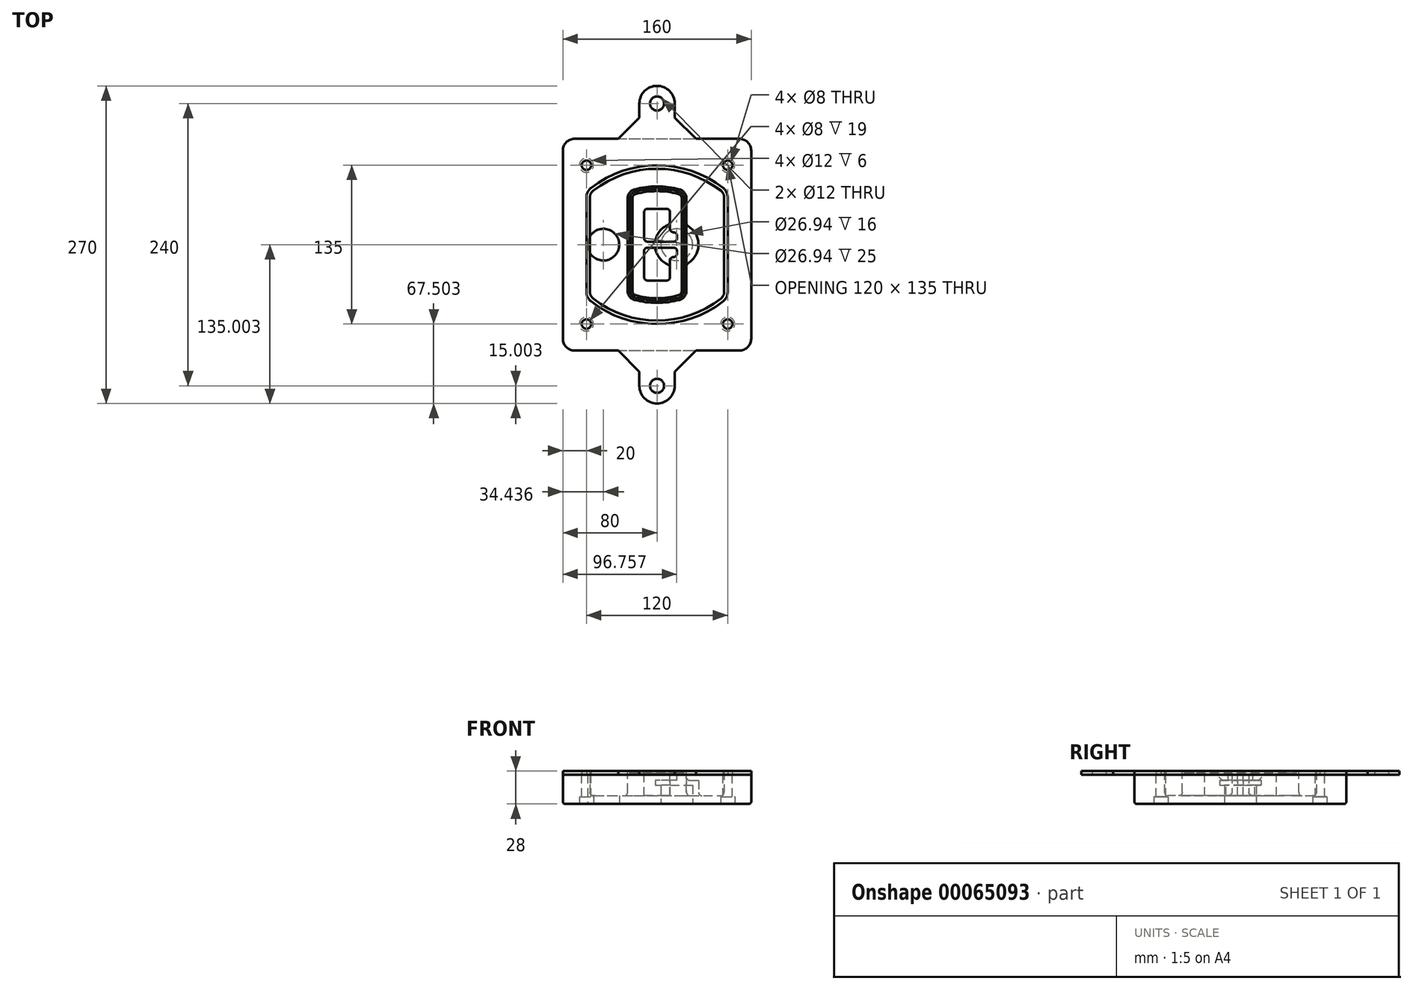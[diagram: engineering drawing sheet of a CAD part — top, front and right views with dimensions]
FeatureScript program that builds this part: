
annotation { "Feature Type Name" : "Feature", "Feature Type Description" : "" }
export const myFeature = defineFeature(function(context is Context, id is Id, definition is map)
    precondition{}
    {
        {
            var Q0;
            Q0=qCreatedBy(makeId("Top.planeOp"),FACE);
            var sketch = newSketch(context, id + "F0", { "sketchPlane" : qUnion([Q0])});
            skPoint(sketch, "E0.rect.middle", {"position": v(0, 0) * mm});
            skLineSegment(sketch, "E1.bottom", {"start": v(24.05, 28.38) * mm, "end": v(164.05, 28.38) * mm});
            skLineSegment(sketch, "E1.top", {"start": v(24.05, 208.38) * mm, "end": v(164.05, 208.38) * mm});
            skLineSegment(sketch, "E1.left", {"start": v(14.05, 38.38) * mm, "end": v(14.05, 198.38) * mm});
            skLineSegment(sketch, "E1.right", {"start": v(174.05, 38.38) * mm, "end": v(174.05, 198.38) * mm});
            skLineSegment(sketch, "E2", {"start": v(14.05, 208.38) * mm, "end": v(174.05, 28.38) * mm, "construction": true});
            skLineSegment(sketch, "E3", {"start": v(174.05, 208.38) * mm, "end": v(14.05, 28.38) * mm, "construction": true});
            skCircle(sketch, "E4", {"center": v(34.05, 185.88) * mm, "radius": 4 * mm});
            skCircle(sketch, "E5", {"center": v(154.05, 185.88) * mm, "radius": 4 * mm});
            skCircle(sketch, "E6", {"center": v(154.05, 50.88) * mm, "radius": 4 * mm});
            skCircle(sketch, "E7", {"center": v(34.05, 50.88) * mm, "radius": 4 * mm});
            skLineSegment(sketch, "E8", {"start": v(34.05, 185.88) * mm, "end": v(154.05, 185.88) * mm, "construction": true});
            skLineSegment(sketch, "E9", {"start": v(154.05, 185.88) * mm, "end": v(154.05, 50.88) * mm, "construction": true});
            skLineSegment(sketch, "E10", {"start": v(154.05, 50.88) * mm, "end": v(34.05, 50.88) * mm, "construction": true});
            skLineSegment(sketch, "E11", {"start": v(34.05, 50.88) * mm, "end": v(34.05, 185.88) * mm, "construction": true});
            skLineSegment(sketch, "E12", {"start": v(34.05, 158.68) * mm, "end": v(34.05, 78.09) * mm});
            skLineSegment(sketch, "E13", {"start": v(154.05, 158.68) * mm, "end": v(154.05, 78.09) * mm});
            skArc(sketch, "E14", {"start": v(150.2, 166.56) * mm, "mid": v(94.05, 185.88) * mm, "end": v(37.9, 166.56) * mm});
            skArc(sketch, "E15", {"start": v(37.9, 70.2) * mm, "mid": v(94.05, 50.88) * mm, "end": v(150.2, 70.2) * mm});
            skLineSegment(sketch, "E16", {"start": v(34.05, 118.38) * mm, "end": v(154.05, 118.38) * mm, "construction": true});
            skPoint(sketch, "E17.visualSharp", {"position": v(34.05, 73.38) * mm});
            skArc(sketch, "E17.filletArc", {"start": v(34.05, 78.09) * mm, "mid": v(35.06, 73.7) * mm, "end": v(37.9, 70.2) * mm});
            skPoint(sketch, "E18.visualSharp", {"position": v(34.05, 163.38) * mm});
            skArc(sketch, "E18.filletArc", {"start": v(37.9, 166.56) * mm, "mid": v(35.06, 163.06) * mm, "end": v(34.05, 158.68) * mm});
            skPoint(sketch, "E19.visualSharp", {"position": v(154.05, 163.38) * mm});
            skArc(sketch, "E19.filletArc", {"start": v(154.05, 158.68) * mm, "mid": v(153.04, 163.06) * mm, "end": v(150.2, 166.56) * mm});
            skPoint(sketch, "E20.visualSharp", {"position": v(154.05, 73.38) * mm});
            skArc(sketch, "E20.filletArc", {"start": v(150.2, 70.2) * mm, "mid": v(153.04, 73.7) * mm, "end": v(154.05, 78.09) * mm});
            skPoint(sketch, "E21.visualSharp", {"position": v(14.05, 208.38) * mm});
            skArc(sketch, "E21.filletArc", {"start": v(24.05, 208.38) * mm, "mid": v(16.98, 205.45) * mm, "end": v(14.05, 198.38) * mm});
            skPoint(sketch, "E22.visualSharp", {"position": v(174.05, 208.38) * mm});
            skArc(sketch, "E22.filletArc", {"start": v(174.05, 198.38) * mm, "mid": v(171.12, 205.45) * mm, "end": v(164.05, 208.38) * mm});
            skPoint(sketch, "E23.visualSharp", {"position": v(174.05, 28.38) * mm});
            skArc(sketch, "E23.filletArc", {"start": v(164.05, 28.38) * mm, "mid": v(171.12, 31.31) * mm, "end": v(174.05, 38.38) * mm});
            skPoint(sketch, "E24.visualSharp", {"position": v(14.05, 28.38) * mm});
            skArc(sketch, "E24.filletArc", {"start": v(14.05, 38.38) * mm, "mid": v(16.98, 31.31) * mm, "end": v(24.05, 28.38) * mm});
            skArc(sketch, "E25.0", {"start": v(151.05, 158.68) * mm, "mid": v(150.34, 161.75) * mm, "end": v(148.36, 164.2) * mm});
            skLineSegment(sketch, "E25.1", {"start": v(151.05, 158.68) * mm, "end": v(151.05, 78.09) * mm});
            skArc(sketch, "E25.2", {"start": v(148.36, 72.57) * mm, "mid": v(150.34, 75.02) * mm, "end": v(151.05, 78.09) * mm});
            skArc(sketch, "E25.3", {"start": v(39.74, 72.57) * mm, "mid": v(94.05, 53.88) * mm, "end": v(148.36, 72.57) * mm});
            skArc(sketch, "E25.4", {"start": v(37.05, 78.09) * mm, "mid": v(37.76, 75.02) * mm, "end": v(39.74, 72.57) * mm});
            skArc(sketch, "E25.5", {"start": v(148.36, 164.2) * mm, "mid": v(94.05, 182.88) * mm, "end": v(39.74, 164.2) * mm});
            skLineSegment(sketch, "E25.6", {"start": v(37.05, 158.68) * mm, "end": v(37.05, 78.09) * mm});
            skArc(sketch, "E25.7", {"start": v(39.74, 164.2) * mm, "mid": v(37.76, 161.75) * mm, "end": v(37.05, 158.68) * mm});
            skArc(sketch, "E26.0", {"start": v(35.43, 169.71) * mm, "mid": v(31.47, 164.82) * mm, "end": v(30.05, 158.68) * mm});
            skArc(sketch, "E26.1", {"start": v(152.67, 169.71) * mm, "mid": v(94.05, 189.88) * mm, "end": v(35.43, 169.71) * mm});
            skArc(sketch, "E26.2", {"start": v(158.05, 158.68) * mm, "mid": v(156.63, 164.82) * mm, "end": v(152.67, 169.71) * mm});
            skLineSegment(sketch, "E26.3", {"start": v(158.05, 158.68) * mm, "end": v(158.05, 78.09) * mm});
            skArc(sketch, "E26.4", {"start": v(152.67, 67.05) * mm, "mid": v(156.63, 71.95) * mm, "end": v(158.05, 78.09) * mm});
            skLineSegment(sketch, "E26.5", {"start": v(30.05, 158.68) * mm, "end": v(30.05, 78.09) * mm});
            skArc(sketch, "E26.6", {"start": v(35.43, 67.05) * mm, "mid": v(94.05, 46.88) * mm, "end": v(152.67, 67.05) * mm});
            skArc(sketch, "E26.7", {"start": v(30.05, 78.09) * mm, "mid": v(31.47, 71.95) * mm, "end": v(35.43, 67.05) * mm});
            skSolve(sketch);
        }
        {
            var Q0;
            Q0=makeQuery(id+"F0.imprint","IMPRINT",FACE,{"disambiguationData":[TD([[makeQuery(id+"F0.imprint","IMPRINT",EDGE,{"derivedFrom":sQuery(id+"F0.wireOp",EDGE,"E1.bottom")}),1.0]])]});
            var Q1;
            Q1=makeQuery(id+"F0.imprint","IMPRINT",FACE,{"disambiguationData":[TD([[makeQuery(id+"F0.imprint","IMPRINT",EDGE,{"derivedFrom":sQuery(id+"F0.wireOp",EDGE,"E12")}),1.0]])]});
            var Q2;
            Q2=makeQuery(id+"F0.imprint","IMPRINT",FACE,{"disambiguationData":[TD([[makeQuery(id+"F0.imprint","IMPRINT",EDGE,{"derivedFrom":sQuery(id+"F0.wireOp",EDGE,"E25.0")}),1.0]])]});
            var Q3;
            Q3=makeQuery(id+"F0.imprint","IMPRINT",FACE,{"disambiguationData":[TD([[makeQuery(id+"F0.imprint","IMPRINT",EDGE,{"derivedFrom":sQuery(id+"F0.wireOp",EDGE,"E12")}),-1.0]])]});
            extrude(context, id + "F1", {"entities" : qUnion([Q0, Q1, Q2, Q3]), "oppositeDirection" : true, "depth" : 25 * mm});
        }
        {
            var Q0;
            Q0=makeQuery(id+"F0.imprint","IMPRINT",FACE,{"disambiguationData":[TD([[makeQuery(id+"F0.imprint","IMPRINT",EDGE,{"derivedFrom":sQuery(id+"F0.wireOp",EDGE,"E12")}),1.0]])]});
            extrude(context, id + "F2", {"entities" : qUnion([Q0]), "operationType" : NewBodyOperationType.ADD, "depth" : 3 * mm});
        }
        {
            var Q0;
            Q0=makeQuery(id+"F0.imprint","IMPRINT",FACE,{"disambiguationData":[TD([[makeQuery(id+"F0.imprint","IMPRINT",EDGE,{"derivedFrom":sQuery(id+"F0.wireOp",EDGE,"E25.0")}),1.0]])]});
            extrude(context, id + "F3", {"entities" : qUnion([Q0]), "operationType" : NewBodyOperationType.REMOVE, "oppositeDirection" : true, "depth" : 18 * mm});
        }
        {
            var Q0;
            Q0=makeQuery(id+"F2.opExtrude","CAP_FACE",FACE,{"disambiguationData":[OSD([sQuery(id+"F0.wireOp",EDGE,"E12"),sQuery(id+"F0.wireOp",EDGE,"E13"),sQuery(id+"F0.wireOp",EDGE,"E14"),sQuery(id+"F0.wireOp",EDGE,"E15"),sQuery(id+"F0.wireOp",EDGE,"E17.filletArc"),sQuery(id+"F0.wireOp",EDGE,"E18.filletArc"),sQuery(id+"F0.wireOp",EDGE,"E19.filletArc"),sQuery(id+"F0.wireOp",EDGE,"E20.filletArc"),sQuery(id+"F0.wireOp",EDGE,"E25.0"),sQuery(id+"F0.wireOp",EDGE,"E25.1"),sQuery(id+"F0.wireOp",EDGE,"E25.2"),sQuery(id+"F0.wireOp",EDGE,"E25.3"),sQuery(id+"F0.wireOp",EDGE,"E25.4"),sQuery(id+"F0.wireOp",EDGE,"E25.5"),sQuery(id+"F0.wireOp",EDGE,"E25.6"),sQuery(id+"F0.wireOp",EDGE,"E25.7")])],"isStart":false});
            var sketch = newSketch(context, id + "F4", { "sketchPlane" : qUnion([Q0])});
            skArc(sketch, "E27.0", {"start": v(74.97, 71.41) * mm, "mid": v(94.05, 68.88) * mm, "end": v(113.13, 71.41) * mm});
            skArc(sketch, "E28.0", {"start": v(113.13, 165.35) * mm, "mid": v(94.05, 167.88) * mm, "end": v(74.97, 165.35) * mm});
            skLineSegment(sketch, "E29", {"start": v(69.05, 157.63) * mm, "end": v(69.05, 79.14) * mm});
            skLineSegment(sketch, "E30", {"start": v(119.05, 157.63) * mm, "end": v(119.05, 79.14) * mm});
            skLineSegment(sketch, "E31", {"start": v(69.05, 163.48) * mm, "end": v(119.05, 163.48) * mm, "construction": true});
            skLineSegment(sketch, "E32", {"start": v(69.05, 73.28) * mm, "end": v(119.05, 73.28) * mm, "construction": true});
            skPoint(sketch, "E33.visualSharp", {"position": v(69.05, 163.48) * mm});
            skArc(sketch, "E33.filletArc", {"start": v(74.97, 165.35) * mm, "mid": v(70.7, 162.5) * mm, "end": v(69.05, 157.63) * mm});
            skPoint(sketch, "E34.visualSharp", {"position": v(119.05, 163.48) * mm});
            skArc(sketch, "E34.filletArc", {"start": v(119.05, 157.63) * mm, "mid": v(117.4, 162.5) * mm, "end": v(113.13, 165.35) * mm});
            skPoint(sketch, "E35.visualSharp", {"position": v(119.05, 73.28) * mm});
            skArc(sketch, "E35.filletArc", {"start": v(113.13, 71.41) * mm, "mid": v(117.4, 74.27) * mm, "end": v(119.05, 79.14) * mm});
            skPoint(sketch, "E36.visualSharp", {"position": v(69.05, 73.28) * mm});
            skArc(sketch, "E36.filletArc", {"start": v(69.05, 79.14) * mm, "mid": v(70.7, 74.27) * mm, "end": v(74.97, 71.41) * mm});
            skArc(sketch, "E37.0", {"start": v(148.36, 164.2) * mm, "mid": v(94.05, 182.88) * mm, "end": v(39.74, 164.2) * mm});
            skArc(sketch, "E37.1", {"start": v(39.74, 164.2) * mm, "mid": v(37.76, 161.75) * mm, "end": v(37.05, 158.68) * mm});
            skLineSegment(sketch, "E37.2", {"start": v(37.05, 158.68) * mm, "end": v(37.05, 78.09) * mm});
            skArc(sketch, "E37.3", {"start": v(37.05, 78.09) * mm, "mid": v(37.76, 75.02) * mm, "end": v(39.74, 72.57) * mm});
            skArc(sketch, "E37.4", {"start": v(39.74, 72.57) * mm, "mid": v(94.05, 53.88) * mm, "end": v(148.36, 72.57) * mm});
            skArc(sketch, "E37.5", {"start": v(148.36, 72.57) * mm, "mid": v(150.34, 75.02) * mm, "end": v(151.05, 78.09) * mm});
            skLineSegment(sketch, "E37.6", {"start": v(151.05, 158.68) * mm, "end": v(151.05, 78.09) * mm});
            skArc(sketch, "E37.7", {"start": v(151.05, 158.68) * mm, "mid": v(150.34, 161.75) * mm, "end": v(148.36, 164.2) * mm});
            skLineSegment(sketch, "E38.0", {"start": v(117.05, 157.63) * mm, "end": v(117.05, 79.14) * mm});
            skArc(sketch, "E38.1", {"start": v(112.61, 73.34) * mm, "mid": v(115.81, 75.49) * mm, "end": v(117.05, 79.14) * mm});
            skArc(sketch, "E38.2", {"start": v(75.49, 73.34) * mm, "mid": v(94.05, 70.88) * mm, "end": v(112.61, 73.34) * mm});
            skArc(sketch, "E38.3", {"start": v(71.05, 79.14) * mm, "mid": v(72.29, 75.49) * mm, "end": v(75.49, 73.34) * mm});
            skLineSegment(sketch, "E38.4", {"start": v(71.05, 157.63) * mm, "end": v(71.05, 79.14) * mm});
            skArc(sketch, "E38.5", {"start": v(117.05, 157.63) * mm, "mid": v(115.81, 161.28) * mm, "end": v(112.61, 163.42) * mm});
            skArc(sketch, "E38.6", {"start": v(75.49, 163.42) * mm, "mid": v(72.29, 161.28) * mm, "end": v(71.05, 157.63) * mm});
            skArc(sketch, "E38.7", {"start": v(112.61, 163.42) * mm, "mid": v(94.05, 165.88) * mm, "end": v(75.49, 163.42) * mm});
            skArc(sketch, "E39.0", {"start": v(115.05, 157.63) * mm, "mid": v(114.23, 160.06) * mm, "end": v(112.1, 161.5) * mm});
            skLineSegment(sketch, "E39.1", {"start": v(115.05, 157.63) * mm, "end": v(115.05, 79.14) * mm});
            skArc(sketch, "E39.2", {"start": v(112.1, 75.27) * mm, "mid": v(114.23, 76.7) * mm, "end": v(115.05, 79.14) * mm});
            skArc(sketch, "E39.3", {"start": v(76, 75.27) * mm, "mid": v(94.05, 72.88) * mm, "end": v(112.1, 75.27) * mm});
            skArc(sketch, "E39.4", {"start": v(73.05, 79.14) * mm, "mid": v(73.87, 76.7) * mm, "end": v(76, 75.27) * mm});
            skArc(sketch, "E39.5", {"start": v(112.1, 161.5) * mm, "mid": v(94.05, 163.88) * mm, "end": v(76, 161.5) * mm});
            skLineSegment(sketch, "E39.6", {"start": v(73.05, 157.63) * mm, "end": v(73.05, 79.14) * mm});
            skArc(sketch, "E39.7", {"start": v(76, 161.5) * mm, "mid": v(73.87, 160.06) * mm, "end": v(73.05, 157.63) * mm});
            skLineSegment(sketch, "E40", {"start": v(69.05, 118.38) * mm, "end": v(119.05, 118.38) * mm, "construction": true});
            skLineSegment(sketch, "E41", {"start": v(83.05, 123.88) * mm, "end": v(83.05, 145.88) * mm});
            skLineSegment(sketch, "E42", {"start": v(86.05, 148.88) * mm, "end": v(102.05, 148.88) * mm});
            skLineSegment(sketch, "E43", {"start": v(105.05, 145.88) * mm, "end": v(105.05, 131.88) * mm});
            skLineSegment(sketch, "E44", {"start": v(108.05, 128.88) * mm, "end": v(108.05, 128.88) * mm});
            skLineSegment(sketch, "E45", {"start": v(111.05, 125.88) * mm, "end": v(111.05, 123.88) * mm});
            skLineSegment(sketch, "E46", {"start": v(108.05, 120.88) * mm, "end": v(86.05, 120.88) * mm});
            skPoint(sketch, "E47.visualSharp", {"position": v(83.05, 148.88) * mm});
            skArc(sketch, "E47.filletArc", {"start": v(86.05, 148.88) * mm, "mid": v(83.93, 148) * mm, "end": v(83.05, 145.88) * mm});
            skPoint(sketch, "E48.visualSharp", {"position": v(105.05, 148.88) * mm});
            skArc(sketch, "E48.filletArc", {"start": v(105.05, 145.88) * mm, "mid": v(104.17, 148) * mm, "end": v(102.05, 148.88) * mm});
            skPoint(sketch, "E49.visualSharp", {"position": v(105.05, 128.88) * mm});
            skArc(sketch, "E49.filletArc", {"start": v(105.05, 131.88) * mm, "mid": v(105.93, 129.76) * mm, "end": v(108.05, 128.88) * mm});
            skPoint(sketch, "E50.visualSharp", {"position": v(111.05, 128.88) * mm});
            skArc(sketch, "E50.filletArc", {"start": v(111.05, 125.88) * mm, "mid": v(110.17, 128) * mm, "end": v(108.05, 128.88) * mm});
            skPoint(sketch, "E51.visualSharp", {"position": v(111.05, 120.88) * mm});
            skArc(sketch, "E51.filletArc", {"start": v(108.05, 120.88) * mm, "mid": v(110.17, 121.76) * mm, "end": v(111.05, 123.88) * mm});
            skPoint(sketch, "E52.visualSharp", {"position": v(83.05, 120.88) * mm});
            skArc(sketch, "E52.filletArc", {"start": v(83.05, 123.88) * mm, "mid": v(83.93, 121.76) * mm, "end": v(86.05, 120.88) * mm});
            skLineSegment(sketch, "E53.0.MirrorCS", {"start": v(108.05, 115.88) * mm, "end": v(86.05, 115.88) * mm});
            skArc(sketch, "E54.0.MirrorCS", {"start": v(83.05, 112.88) * mm, "mid": v(83.93, 115) * mm, "end": v(86.05, 115.88) * mm});
            skLineSegment(sketch, "E55.0.MirrorCS", {"start": v(83.05, 112.88) * mm, "end": v(83.05, 90.88) * mm});
            skArc(sketch, "E56.0.MirrorCS", {"start": v(86.05, 87.88) * mm, "mid": v(83.93, 88.76) * mm, "end": v(83.05, 90.88) * mm});
            skLineSegment(sketch, "E57.0.MirrorCS", {"start": v(86.05, 87.88) * mm, "end": v(102.05, 87.88) * mm});
            skArc(sketch, "E58.0.MirrorCS", {"start": v(105.05, 90.88) * mm, "mid": v(104.17, 88.76) * mm, "end": v(102.05, 87.88) * mm});
            skLineSegment(sketch, "E59.0.MirrorCS", {"start": v(105.05, 90.88) * mm, "end": v(105.05, 104.88) * mm});
            skArc(sketch, "E60.0.MirrorCS", {"start": v(105.05, 104.88) * mm, "mid": v(105.93, 107) * mm, "end": v(108.05, 107.88) * mm});
            skArc(sketch, "E61.0.MirrorCS", {"start": v(111.05, 110.88) * mm, "mid": v(110.17, 108.76) * mm, "end": v(108.05, 107.88) * mm});
            skLineSegment(sketch, "E62.0.MirrorCS", {"start": v(111.05, 110.88) * mm, "end": v(111.05, 112.88) * mm});
            skArc(sketch, "E63.0.MirrorCS", {"start": v(108.05, 115.88) * mm, "mid": v(110.17, 115) * mm, "end": v(111.05, 112.88) * mm});
            skSolve(sketch);
        }
        {
            var Q0;
            Q0=makeQuery(id+"F4.imprint","IMPRINT",FACE,{"disambiguationData":[TD([[makeQuery(id+"F4.imprint","IMPRINT",EDGE,{"derivedFrom":sQuery(id+"F4.wireOp",EDGE,"E27.0")}),1.0]])]});
            var Q1;
            Q1=makeQuery(id+"F4.imprint","IMPRINT",FACE,{"disambiguationData":[TD([[makeQuery(id+"F4.imprint","IMPRINT",EDGE,{"derivedFrom":sQuery(id+"F4.wireOp",EDGE,"E38.0")}),-1.0]])]});
            var Q2;
            Q2=makeQuery(id+"F4.imprint","IMPRINT",FACE,{"disambiguationData":[TD([[makeQuery(id+"F4.imprint","IMPRINT",EDGE,{"derivedFrom":sQuery(id+"F4.wireOp",EDGE,"E39.0")}),1.0]])]});
            extrude(context, id + "F5", {"entities" : qUnion([Q0, Q1, Q2]), "operationType" : NewBodyOperationType.ADD, "endBound" : BoundingType.UP_TO_NEXT, "oppositeDirection" : true, "depth" : 25 * mm});
        }
        {
            var Q0;
            Q0=makeQuery(id+"F4.imprint","IMPRINT",FACE,{"disambiguationData":[TD([[makeQuery(id+"F4.imprint","IMPRINT",EDGE,{"derivedFrom":sQuery(id+"F4.wireOp",EDGE,"E38.0")}),-1.0]])]});
            extrude(context, id + "F6", {"entities" : qUnion([Q0]), "operationType" : NewBodyOperationType.REMOVE, "oppositeDirection" : true, "depth" : 2 * mm});
        }
        {
            var Q0;
            Q0=makeQuery(id+"F1.opExtrude","CAP_FACE",FACE,{"disambiguationData":[OSD([sQuery(id+"F0.wireOp",EDGE,"E1.bottom"),sQuery(id+"F0.wireOp",EDGE,"E1.top"),sQuery(id+"F0.wireOp",EDGE,"E1.left"),sQuery(id+"F0.wireOp",EDGE,"E1.right"),sQuery(id+"F0.wireOp",EDGE,"E4"),sQuery(id+"F0.wireOp",EDGE,"E5"),sQuery(id+"F0.wireOp",EDGE,"E6"),sQuery(id+"F0.wireOp",EDGE,"E7"),sQuery(id+"F0.wireOp",EDGE,"E21.filletArc"),sQuery(id+"F0.wireOp",EDGE,"E22.filletArc"),sQuery(id+"F0.wireOp",EDGE,"E23.filletArc"),sQuery(id+"F0.wireOp",EDGE,"E24.filletArc")])],"isStart":false});
            var sketch = newSketch(context, id + "F7", { "sketchPlane" : qUnion([Q0])});
            skCircle(sketch, "E64", {"center": v(110.8, -118.38) * mm, "radius": 13.47 * mm});
            skCircle(sketch, "E65", {"center": v(48.49, -118.38) * mm, "radius": 13.47 * mm});
            skLineSegment(sketch, "E66", {"start": v(174.05, -118.38) * mm, "end": v(14.05, -118.38) * mm});
            skCircle(sketch, "E67", {"center": v(110.8, -118.38) * mm, "radius": 18.47 * mm});
            skCircle(sketch, "E68", {"center": v(154.05, -185.88) * mm, "radius": 6 * mm});
            skCircle(sketch, "E69", {"center": v(34.05, -185.88) * mm, "radius": 6 * mm});
            skCircle(sketch, "E70", {"center": v(34.05, -50.88) * mm, "radius": 6 * mm});
            skCircle(sketch, "E71", {"center": v(154.05, -50.88) * mm, "radius": 6 * mm});
            skSolve(sketch);
        }
        {
            var Q0;
            {var subQ1=sQuery(id+"F7.wireOp",EDGE,"E66");var subQ4=sQuery(id+"F7.wireOp",EDGE,"E64");var subQ6=makeQuery(id+"F7.imprint","INTERSECT",VERTEX,{"disambiguationData":[OD(0.0)],"derivedFrom":[subQ4,subQ1]});Q0=makeQuery(id+"F7.imprint","IMPRINT",FACE,{"disambiguationData":[TD([[makeQuery(id+"F7.imprint","IMPRINT",EDGE,{"disambiguationData":[TD([[subQ6,-1.0]])],"derivedFrom":subQ4}),-1.0]])]});}
            var Q1;
            {var subQ0=sQuery(id+"F7.wireOp",EDGE,"E66");var subQ1=sQuery(id+"F7.wireOp",EDGE,"E64");var subQ3=makeQuery(id+"F7.imprint","INTERSECT",VERTEX,{"disambiguationData":[OD(0.0)],"derivedFrom":[subQ1,subQ0]});Q1=makeQuery(id+"F7.imprint","IMPRINT",FACE,{"disambiguationData":[TD([[makeQuery(id+"F7.imprint","IMPRINT",EDGE,{"disambiguationData":[TD([[subQ3,-1.0]])],"derivedFrom":subQ1}),1.0]])]});}
            var Q2;
            {var subQ0=sQuery(id+"F7.wireOp",EDGE,"E66");var subQ1=sQuery(id+"F7.wireOp",EDGE,"E64");var subQ3=makeQuery(id+"F7.imprint","INTERSECT",VERTEX,{"disambiguationData":[OD(0.0)],"derivedFrom":[subQ1,subQ0]});Q2=makeQuery(id+"F7.imprint","IMPRINT",FACE,{"disambiguationData":[TD([[makeQuery(id+"F7.imprint","IMPRINT",EDGE,{"disambiguationData":[TD([[subQ3,1.0]])],"derivedFrom":subQ1}),1.0]])]});}
            var Q3;
            {var subQ1=sQuery(id+"F7.wireOp",EDGE,"E66");var subQ4=sQuery(id+"F7.wireOp",EDGE,"E64");var subQ6=makeQuery(id+"F7.imprint","INTERSECT",VERTEX,{"disambiguationData":[OD(0.0)],"derivedFrom":[subQ4,subQ1]});Q3=makeQuery(id+"F7.imprint","IMPRINT",FACE,{"disambiguationData":[TD([[makeQuery(id+"F7.imprint","IMPRINT",EDGE,{"disambiguationData":[TD([[subQ6,1.0]])],"derivedFrom":subQ4}),-1.0]])]});}
            extrude(context, id + "F8", {"entities" : qUnion([Q0, Q1, Q2, Q3]), "operationType" : NewBodyOperationType.ADD, "oppositeDirection" : true, "depth" : 20 * mm});
        }
        {
            var Q0;
            {var subQ0=sQuery(id+"F7.wireOp",EDGE,"E66");var subQ1=sQuery(id+"F7.wireOp",EDGE,"E64");var subQ3=makeQuery(id+"F7.imprint","INTERSECT",VERTEX,{"disambiguationData":[OD(0.0)],"derivedFrom":[subQ1,subQ0]});Q0=makeQuery(id+"F7.imprint","IMPRINT",FACE,{"disambiguationData":[TD([[makeQuery(id+"F7.imprint","IMPRINT",EDGE,{"disambiguationData":[TD([[subQ3,-1.0]])],"derivedFrom":subQ1}),1.0]])]});}
            var Q1;
            {var subQ0=sQuery(id+"F7.wireOp",EDGE,"E66");var subQ1=sQuery(id+"F7.wireOp",EDGE,"E64");var subQ3=makeQuery(id+"F7.imprint","INTERSECT",VERTEX,{"disambiguationData":[OD(0.0)],"derivedFrom":[subQ1,subQ0]});Q1=makeQuery(id+"F7.imprint","IMPRINT",FACE,{"disambiguationData":[TD([[makeQuery(id+"F7.imprint","IMPRINT",EDGE,{"disambiguationData":[TD([[subQ3,1.0]])],"derivedFrom":subQ1}),1.0]])]});}
            extrude(context, id + "F9", {"entities" : qUnion([Q0, Q1]), "operationType" : NewBodyOperationType.REMOVE, "oppositeDirection" : true, "depth" : 16 * mm});
        }
        {
            var Q0;
            {var subQ0=sQuery(id+"F7.wireOp",EDGE,"E66");var subQ1=sQuery(id+"F7.wireOp",EDGE,"E65");var subQ3=makeQuery(id+"F7.imprint","INTERSECT",VERTEX,{"disambiguationData":[OD(0.0)],"derivedFrom":[subQ1,subQ0]});Q0=makeQuery(id+"F7.imprint","IMPRINT",FACE,{"disambiguationData":[TD([[makeQuery(id+"F7.imprint","IMPRINT",EDGE,{"disambiguationData":[TD([[subQ3,-1.0]])],"derivedFrom":subQ1}),1.0]])]});}
            var Q1;
            {var subQ0=sQuery(id+"F7.wireOp",EDGE,"E66");var subQ1=sQuery(id+"F7.wireOp",EDGE,"E65");var subQ3=makeQuery(id+"F7.imprint","INTERSECT",VERTEX,{"disambiguationData":[OD(0.0)],"derivedFrom":[subQ1,subQ0]});Q1=makeQuery(id+"F7.imprint","IMPRINT",FACE,{"disambiguationData":[TD([[makeQuery(id+"F7.imprint","IMPRINT",EDGE,{"disambiguationData":[TD([[subQ3,1.0]])],"derivedFrom":subQ1}),1.0]])]});}
            extrude(context, id + "F10", {"entities" : qUnion([Q0, Q1]), "operationType" : NewBodyOperationType.REMOVE, "oppositeDirection" : true, "depth" : 25 * mm});
        }
        {
            var Q0;
            Q0=makeQuery(id+"F7.imprint","IMPRINT",FACE,{"disambiguationData":[TD([[makeQuery(id+"F7.imprint","IMPRINT",EDGE,{"derivedFrom":sQuery(id+"F7.wireOp",EDGE,"E68")}),1.0]])]});
            var Q1;
            Q1=makeQuery(id+"F7.imprint","IMPRINT",FACE,{"disambiguationData":[TD([[makeQuery(id+"F7.imprint","IMPRINT",EDGE,{"derivedFrom":makeQuery(id+"F1.opExtrude","CAP_EDGE",EDGE,{"disambiguationData":[OSD([sQuery(id+"F0.wireOp",EDGE,"E5")])],"isStart":false})}),-1.0]])]});
            var Q2;
            Q2=makeQuery(id+"F7.imprint","IMPRINT",FACE,{"disambiguationData":[TD([[makeQuery(id+"F7.imprint","IMPRINT",EDGE,{"derivedFrom":sQuery(id+"F7.wireOp",EDGE,"E69")}),1.0]])]});
            var Q3;
            Q3=makeQuery(id+"F7.imprint","IMPRINT",FACE,{"disambiguationData":[TD([[makeQuery(id+"F7.imprint","IMPRINT",EDGE,{"derivedFrom":makeQuery(id+"F1.opExtrude","CAP_EDGE",EDGE,{"disambiguationData":[OSD([sQuery(id+"F0.wireOp",EDGE,"E4")])],"isStart":false})}),-1.0]])]});
            var Q4;
            Q4=makeQuery(id+"F7.imprint","IMPRINT",FACE,{"disambiguationData":[TD([[makeQuery(id+"F7.imprint","IMPRINT",EDGE,{"derivedFrom":sQuery(id+"F7.wireOp",EDGE,"E70")}),1.0]])]});
            var Q5;
            Q5=makeQuery(id+"F7.imprint","IMPRINT",FACE,{"disambiguationData":[TD([[makeQuery(id+"F7.imprint","IMPRINT",EDGE,{"derivedFrom":makeQuery(id+"F1.opExtrude","CAP_EDGE",EDGE,{"disambiguationData":[OSD([sQuery(id+"F0.wireOp",EDGE,"E7")])],"isStart":false})}),-1.0]])]});
            var Q6;
            Q6=makeQuery(id+"F7.imprint","IMPRINT",FACE,{"disambiguationData":[TD([[makeQuery(id+"F7.imprint","IMPRINT",EDGE,{"derivedFrom":sQuery(id+"F7.wireOp",EDGE,"E71")}),1.0]])]});
            var Q7;
            Q7=makeQuery(id+"F7.imprint","IMPRINT",FACE,{"disambiguationData":[TD([[makeQuery(id+"F7.imprint","IMPRINT",EDGE,{"derivedFrom":makeQuery(id+"F1.opExtrude","CAP_EDGE",EDGE,{"disambiguationData":[OSD([sQuery(id+"F0.wireOp",EDGE,"E6")])],"isStart":false})}),-1.0]])]});
            extrude(context, id + "F11", {"entities" : qUnion([Q0, Q1, Q2, Q3, Q4, Q5, Q6, Q7]), "operationType" : NewBodyOperationType.REMOVE, "oppositeDirection" : true, "depth" : 6 * mm});
        }
        {
            var Q0;
            Q0=makeQuery(id+"F9.boolean.opBoolean","COPY",FACE,{"derivedFrom":makeQuery(id+"F9.opExtrude","CAP_FACE",FACE,{"disambiguationData":[OSD([sQuery(id+"F7.wireOp",EDGE,"E64")])],"isStart":false})});
            var sketch = newSketch(context, id + "F12", { "sketchPlane" : qUnion([Q0])});
            skArc(sketch, "E72.0", {"start": v(105.05, -100.83) * mm, "mid": v(96.62, -106.56) * mm, "end": v(92.5, -115.88) * mm});
            skArc(sketch, "E72.1", {"start": v(92.5, -120.88) * mm, "mid": v(96.62, -130.2) * mm, "end": v(105.05, -135.93) * mm});
            skLineSegment(sketch, "E73", {"start": v(92.5, -120.88) * mm, "end": v(108.05, -120.88) * mm});
            skLineSegment(sketch, "E74.0", {"start": v(108.05, -115.88) * mm, "end": v(92.5, -115.88) * mm});
            skArc(sketch, "E74.1", {"start": v(108.05, -115.88) * mm, "mid": v(110.17, -115) * mm, "end": v(111.05, -112.88) * mm});
            skLineSegment(sketch, "E74.2", {"start": v(111.05, -110.88) * mm, "end": v(111.05, -112.88) * mm});
            skArc(sketch, "E74.3", {"start": v(111.05, -110.88) * mm, "mid": v(110.17, -108.76) * mm, "end": v(108.05, -107.88) * mm});
            skArc(sketch, "E74.4", {"start": v(105.05, -104.88) * mm, "mid": v(105.93, -107) * mm, "end": v(108.05, -107.88) * mm});
            skLineSegment(sketch, "E74.5", {"start": v(105.05, -100.83) * mm, "end": v(105.05, -104.88) * mm});
            skLineSegment(sketch, "E74.7", {"start": v(108.05, -120.88) * mm, "end": v(92.5, -120.88) * mm});
            skArc(sketch, "E74.8", {"start": v(108.05, -120.88) * mm, "mid": v(110.17, -121.76) * mm, "end": v(111.05, -123.88) * mm});
            skLineSegment(sketch, "E74.9", {"start": v(111.05, -125.88) * mm, "end": v(111.05, -123.88) * mm});
            skArc(sketch, "E74.10", {"start": v(111.05, -125.88) * mm, "mid": v(110.17, -128) * mm, "end": v(108.05, -128.88) * mm});
            skArc(sketch, "E74.11", {"start": v(105.05, -131.88) * mm, "mid": v(105.93, -129.76) * mm, "end": v(108.05, -128.88) * mm});
            skLineSegment(sketch, "E74.12", {"start": v(105.05, -135.93) * mm, "end": v(105.05, -131.88) * mm});
            skPoint(sketch, "E75.orphan", {"position": v(105.05, -145.88) * mm});
            skPoint(sketch, "E76.orphan", {"position": v(86.05, -120.88) * mm});
            skPoint(sketch, "E77.orphan", {"position": v(86.05, -115.88) * mm});
            skPoint(sketch, "E78.orphan", {"position": v(105.05, -90.88) * mm});
            skSolve(sketch);
        }
        {
            var Q0;
            {var subQ7=sQuery(id+"F12.wireOp",EDGE,"E72.0");var subQ14=sQuery(id+"F12.wireOp",EDGE,"E72.1");var subQ16=sQuery(id+"F12.wireOp",EDGE,"E74.1");var subQ18=sQuery(id+"F12.wireOp",EDGE,"E74.8");Q0=qUnion([makeQuery(id+"F12.imprint","IMPRINT",FACE,{"disambiguationData":[TD([[makeQuery(id+"F12.imprint","IMPRINT",EDGE,{"derivedFrom":subQ7}),1.0]])]}),makeQuery(id+"F12.imprint","IMPRINT",FACE,{"disambiguationData":[TD([[makeQuery(id+"F12.imprint","IMPRINT",EDGE,{"derivedFrom":subQ14}),1.0]])]}),makeQuery(id+"F12.imprint","IMPRINT",FACE,{"disambiguationData":[TD([[makeQuery(id+"F12.imprint","IMPRINT",EDGE,{"derivedFrom":subQ16}),1.0]])]}),makeQuery(id+"F12.imprint","IMPRINT",FACE,{"disambiguationData":[TD([[makeQuery(id+"F12.imprint","IMPRINT",EDGE,{"derivedFrom":subQ18}),-1.0]])]})]);}
            var Q1;
            Q1=makeQuery(id+"F5.boolean.opBoolean","SPLIT",FACE,{"disambiguationData":[TD([makeQuery(id+"F5.opExtrude","SWEPT_FACE",FACE,{"disambiguationData":[OSD([sQuery(id+"F4.wireOp",EDGE,"E41")])]})])],"derivedFrom":makeQuery(id+"F3.boolean.opBoolean","COPY",FACE,{"derivedFrom":makeQuery(id+"F3.opExtrude","CAP_FACE",FACE,{"disambiguationData":[OSD([sQuery(id+"F0.wireOp",EDGE,"E25.0"),sQuery(id+"F0.wireOp",EDGE,"E25.1"),sQuery(id+"F0.wireOp",EDGE,"E25.2"),sQuery(id+"F0.wireOp",EDGE,"E25.3"),sQuery(id+"F0.wireOp",EDGE,"E25.4"),sQuery(id+"F0.wireOp",EDGE,"E25.5"),sQuery(id+"F0.wireOp",EDGE,"E25.6"),sQuery(id+"F0.wireOp",EDGE,"E25.7")])],"isStart":false})})});
            extrude(context, id + "F13", {"entities" : qUnion([Q0]), "operationType" : NewBodyOperationType.REMOVE, "endBound" : BoundingType.UP_TO_SURFACE, "endBoundEntityFace" : qUnion([Q1]), "depth" : 25 * mm});
        }
        {
            var Q0;
            Q0=makeQuery(id+"F3.boolean.opBoolean","COPY",EDGE,{"derivedFrom":makeQuery(id+"F3.opExtrude","CAP_EDGE",EDGE,{"disambiguationData":[OSD([sQuery(id+"F0.wireOp",EDGE,"E25.6")])],"isStart":false})});
            var Q1;
            Q1=makeQuery(id+"F8.boolean.opBoolean","INTERSECT",EDGE,{"derivedFrom":[makeQuery(id+"F5.opExtrude","SWEPT_FACE",FACE,{"disambiguationData":[OSD([sQuery(id+"F4.wireOp",EDGE,"E30")])]}),makeQuery(id+"F8.opExtrude","CAP_FACE",FACE,{"disambiguationData":[OSD([sQuery(id+"F7.wireOp",EDGE,"E67")])],"isStart":false})]});
            var Q2;
            Q2=makeQuery(id+"F8.boolean.opBoolean","INTERSECT",EDGE,{"disambiguationData":[OD(1.0)],"derivedFrom":[makeQuery(id+"F5.opExtrude","SWEPT_FACE",FACE,{"disambiguationData":[OSD([sQuery(id+"F4.wireOp",EDGE,"E30")])]}),makeQuery(id+"F8.opExtrude","SWEPT_FACE",FACE,{"disambiguationData":[OSD([sQuery(id+"F7.wireOp",EDGE,"E67")])]})]});
            var Q3;
            {var subQ0=sQuery(id+"F4.wireOp",EDGE,"E30");Q3=makeQuery(id+"F8.boolean.opBoolean","SPLIT",EDGE,{"disambiguationData":[TD([makeQuery(id+"F5.opExtrude","SWEPT_FACE",FACE,{"disambiguationData":[OSD([sQuery(id+"F4.wireOp",EDGE,"E35.filletArc")])]})])],"derivedFrom":makeQuery(id+"F5.opExtrude","CAP_EDGE",EDGE,{"disambiguationData":[OSD([subQ0])],"isStart":false})});}
            var Q4;
            {var subQ0=sQuery(id+"F0.wireOp",EDGE,"E25.7");var subQ1=sQuery(id+"F0.wireOp",EDGE,"E25.1");var subQ2=sQuery(id+"F0.wireOp",EDGE,"E25.6");var subQ3=sQuery(id+"F0.wireOp",EDGE,"E25.5");var subQ4=sQuery(id+"F0.wireOp",EDGE,"E25.4");var subQ5=sQuery(id+"F0.wireOp",EDGE,"E25.0");var subQ6=sQuery(id+"F0.wireOp",EDGE,"E25.2");var subQ7=sQuery(id+"F0.wireOp",EDGE,"E25.3");Q4=makeQuery(id+"F8.boolean.opBoolean","INTERSECT",EDGE,{"derivedFrom":[makeQuery(id+"F5.boolean.opBoolean","SPLIT",FACE,{"disambiguationData":[TD([makeQuery(id+"F2.opExtrude","SWEPT_FACE",FACE,{"disambiguationData":[OSD([subQ5])]})])],"derivedFrom":makeQuery(id+"F3.boolean.opBoolean","COPY",FACE,{"derivedFrom":makeQuery(id+"F3.opExtrude","CAP_FACE",FACE,{"disambiguationData":[OSD([subQ5,subQ1,subQ6,subQ7,subQ4,subQ3,subQ2,subQ0])],"isStart":false})})}),makeQuery(id+"F8.opExtrude","SWEPT_FACE",FACE,{"disambiguationData":[OSD([sQuery(id+"F7.wireOp",EDGE,"E67")])]})]});}
            var Q5;
            Q5=makeQuery(id+"F8.boolean.opBoolean","INTERSECT",EDGE,{"disambiguationData":[OD(0.0)],"derivedFrom":[makeQuery(id+"F5.opExtrude","SWEPT_FACE",FACE,{"disambiguationData":[OSD([sQuery(id+"F4.wireOp",EDGE,"E30")])]}),makeQuery(id+"F8.opExtrude","SWEPT_FACE",FACE,{"disambiguationData":[OSD([sQuery(id+"F7.wireOp",EDGE,"E67")])]})]});
            fillet(context, id + "F14", {"entities" : qUnion([Q0, Q1, Q2, Q3, Q4, Q5]), "radius" : 3 * mm, "tangentPropagation" : true, "allowEdgeOverflow" : false});
        }
        {
            var Q0;
            Q0=makeQuery(id+"F1.opExtrude","CAP_EDGE",EDGE,{"disambiguationData":[OSD([sQuery(id+"F0.wireOp",EDGE,"E1.bottom")])],"isStart":false});
            fillet(context, id + "F15", {"entities" : qUnion([Q0]), "radius" : 2 * mm, "tangentPropagation" : true, "allowEdgeOverflow" : false});
        }
        {
            var Q0;
            {var subQ0=sQuery(id+"F0.wireOp",EDGE,"E22.filletArc");var subQ1=sQuery(id+"F0.wireOp",EDGE,"E7");var subQ2=sQuery(id+"F0.wireOp",EDGE,"E6");var subQ3=sQuery(id+"F0.wireOp",EDGE,"E5");var subQ4=sQuery(id+"F0.wireOp",EDGE,"E4");var subQ5=sQuery(id+"F0.wireOp",EDGE,"E1.bottom");var subQ6=sQuery(id+"F0.wireOp",EDGE,"E21.filletArc");var subQ7=sQuery(id+"F0.wireOp",EDGE,"E1.top");var subQ8=sQuery(id+"F0.wireOp",EDGE,"E1.left");var subQ9=sQuery(id+"F0.wireOp",EDGE,"E1.right");var subQ10=sQuery(id+"F0.wireOp",EDGE,"E23.filletArc");var subQ11=sQuery(id+"F0.wireOp",EDGE,"E24.filletArc");Q0=makeQuery(id+"F2.boolean.opBoolean","SPLIT",FACE,{"disambiguationData":[TD([makeQuery(id+"F1.opExtrude","SWEPT_FACE",FACE,{"disambiguationData":[OSD([subQ5])]})])],"derivedFrom":makeQuery(id+"F1.opExtrude","CAP_FACE",FACE,{"disambiguationData":[OSD([subQ5,subQ7,subQ8,subQ9,subQ4,subQ3,subQ2,subQ1,subQ6,subQ0,subQ10,subQ11])],"isStart":true})});}
            var sketch = newSketch(context, id + "F16", { "sketchPlane" : qUnion([Q0])});
            skArc(sketch, "E79.0", {"start": v(164.05, 28.38) * mm, "mid": v(171.12, 31.31) * mm, "end": v(174.05, 38.38) * mm});
            skCircle(sketch, "E79.1", {"center": v(154.05, 50.88) * mm, "radius": 4 * mm});
            skArc(sketch, "E79.2", {"start": v(150.2, 70.2) * mm, "mid": v(153.04, 73.7) * mm, "end": v(154.05, 78.09) * mm});
            skArc(sketch, "E79.3", {"start": v(37.9, 70.2) * mm, "mid": v(94.05, 50.88) * mm, "end": v(150.2, 70.2) * mm});
            skLineSegment(sketch, "E79.4", {"start": v(24.05, 28.38) * mm, "end": v(164.05, 28.38) * mm});
            skLineSegment(sketch, "E79.5", {"start": v(174.05, 38.38) * mm, "end": v(174.05, 198.38) * mm});
            skLineSegment(sketch, "E79.6", {"start": v(154.05, 158.68) * mm, "end": v(154.05, 78.09) * mm});
            skArc(sketch, "E79.7", {"start": v(154.05, 158.68) * mm, "mid": v(153.04, 163.06) * mm, "end": v(150.2, 166.56) * mm});
            skArc(sketch, "E79.8", {"start": v(150.2, 166.56) * mm, "mid": v(94.05, 185.88) * mm, "end": v(37.9, 166.56) * mm});
            skCircle(sketch, "E79.9", {"center": v(154.05, 185.88) * mm, "radius": 4 * mm});
            skArc(sketch, "E79.10", {"start": v(174.05, 198.38) * mm, "mid": v(171.12, 205.45) * mm, "end": v(164.05, 208.38) * mm});
            skLineSegment(sketch, "E79.11", {"start": v(24.05, 208.38) * mm, "end": v(164.05, 208.38) * mm});
            skCircle(sketch, "E79.12", {"center": v(34.05, 185.88) * mm, "radius": 4 * mm});
            skArc(sketch, "E79.13", {"start": v(37.9, 166.56) * mm, "mid": v(35.06, 163.06) * mm, "end": v(34.05, 158.68) * mm});
            skArc(sketch, "E79.14", {"start": v(24.05, 208.38) * mm, "mid": v(16.98, 205.45) * mm, "end": v(14.05, 198.38) * mm});
            skLineSegment(sketch, "E79.15", {"start": v(14.05, 38.38) * mm, "end": v(14.05, 198.38) * mm});
            skLineSegment(sketch, "E79.16", {"start": v(34.05, 158.68) * mm, "end": v(34.05, 78.09) * mm});
            skArc(sketch, "E79.17", {"start": v(34.05, 78.09) * mm, "mid": v(35.06, 73.7) * mm, "end": v(37.9, 70.2) * mm});
            skCircle(sketch, "E79.18", {"center": v(34.05, 50.88) * mm, "radius": 4 * mm});
            skArc(sketch, "E79.19", {"start": v(14.05, 38.38) * mm, "mid": v(16.98, 31.31) * mm, "end": v(24.05, 28.38) * mm});
            skCircle(sketch, "E80", {"center": v(94.05, 238.38) * mm, "radius": 6 * mm});
            skArc(sketch, "E81", {"start": v(109.05, 238.38) * mm, "mid": v(94.05, 253.38) * mm, "end": v(79.05, 238.38) * mm});
            skLineSegment(sketch, "E82", {"start": v(79.05, 238.38) * mm, "end": v(79.05, 226.38) * mm});
            skLineSegment(sketch, "E83", {"start": v(79.05, 226.38) * mm, "end": v(61.05, 208.38) * mm});
            skLineSegment(sketch, "E84", {"start": v(109.05, 238.38) * mm, "end": v(109.05, 226.38) * mm});
            skLineSegment(sketch, "E85", {"start": v(109.05, 226.38) * mm, "end": v(127.05, 208.38) * mm});
            skLineSegment(sketch, "E86", {"start": v(94.05, 238.38) * mm, "end": v(94.05, 208.38) * mm, "construction": true});
            skPoint(sketch, "E87", {"position": v(94.05, 208.38) * mm});
            skLineSegment(sketch, "E88", {"start": v(14.05, 118.38) * mm, "end": v(174.05, 118.38) * mm, "construction": true});
            skCircle(sketch, "E89.MirrorC", {"center": v(94.05, -1.62) * mm, "radius": 6 * mm});
            skLineSegment(sketch, "E90.MirrorCS", {"start": v(109.05, -1.62) * mm, "end": v(109.05, 10.38) * mm});
            skLineSegment(sketch, "E91.MirrorCS", {"start": v(79.05, -1.62) * mm, "end": v(79.05, 10.38) * mm});
            skLineSegment(sketch, "E92.MirrorCS", {"start": v(94.05, -1.62) * mm, "end": v(94.05, 28.38) * mm, "construction": true});
            skLineSegment(sketch, "E93.MirrorCS", {"start": v(79.05, 10.38) * mm, "end": v(61.05, 28.38) * mm});
            skArc(sketch, "E94.MirrorCS", {"start": v(109.05, -1.62) * mm, "mid": v(94.05, -16.62) * mm, "end": v(79.05, -1.62) * mm});
            skLineSegment(sketch, "E95.MirrorCS", {"start": v(109.05, 10.38) * mm, "end": v(127.05, 28.38) * mm});
            skSolve(sketch);
        }
        {
            var Q0;
            Q0 = qSketchRegion(id + "F16", true);
            var Q1;
            Q1=makeQuery(id+"F2.opExtrude","CAP_FACE",FACE,{"disambiguationData":[OSD([sQuery(id+"F0.wireOp",EDGE,"E12"),sQuery(id+"F0.wireOp",EDGE,"E13"),sQuery(id+"F0.wireOp",EDGE,"E14"),sQuery(id+"F0.wireOp",EDGE,"E15"),sQuery(id+"F0.wireOp",EDGE,"E17.filletArc"),sQuery(id+"F0.wireOp",EDGE,"E18.filletArc"),sQuery(id+"F0.wireOp",EDGE,"E19.filletArc"),sQuery(id+"F0.wireOp",EDGE,"E20.filletArc"),sQuery(id+"F0.wireOp",EDGE,"E25.0"),sQuery(id+"F0.wireOp",EDGE,"E25.1"),sQuery(id+"F0.wireOp",EDGE,"E25.2"),sQuery(id+"F0.wireOp",EDGE,"E25.3"),sQuery(id+"F0.wireOp",EDGE,"E25.4"),sQuery(id+"F0.wireOp",EDGE,"E25.5"),sQuery(id+"F0.wireOp",EDGE,"E25.6"),sQuery(id+"F0.wireOp",EDGE,"E25.7")])],"isStart":false});
            extrude(context, id + "F17", {"entities" : qUnion([Q0]), "endBound" : BoundingType.UP_TO_SURFACE, "endBoundEntityFace" : qUnion([Q1]), "depth" : 25 * mm});
        }
    });
